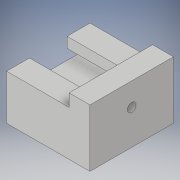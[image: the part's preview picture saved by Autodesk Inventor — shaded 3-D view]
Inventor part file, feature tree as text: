
AUTODESK INVENTOR PART (.ipt)
format: ipt  version: 2019 (Build 230136000, 136)  size: 135,168 bytes
history: native  units: in
note: dims shown in document units (in); Inventor stores cm internally (conversion verified against a paired STEP export)
features: extrude x3, sketch x3
ambient origin geometry x8: Origin, YZ Plane, XZ Plane, XY Plane, X Axis, Y Axis, Z Axis, Center Point
bodies: Solid1 (feature_tree)
feature tree (6):
  extrude  "Extrusion1"  Depth=0.45in
  extrude  "Extrusion2"  Depth=0.15in
  extrude  "Extrusion3"  Depth=0.125in
  sketch  "Sketch1"  dims[d0=1.0in d1=0.45in]
  sketch  "Sketch2"  dims[d2=0.75in d3=0.15in]
  sketch  "Sketch4"  dims[d4=0.275in d5=0.125in d6=0.25in d7=0.54in d8=0.75in d9=0.0in d10=0.15in d11=1.0in d12=0.25in d13=0.0in d21=0.104in d22=0.5in d23=0.125in d24=-0.0in d25=1.0in d26=0.0in]
